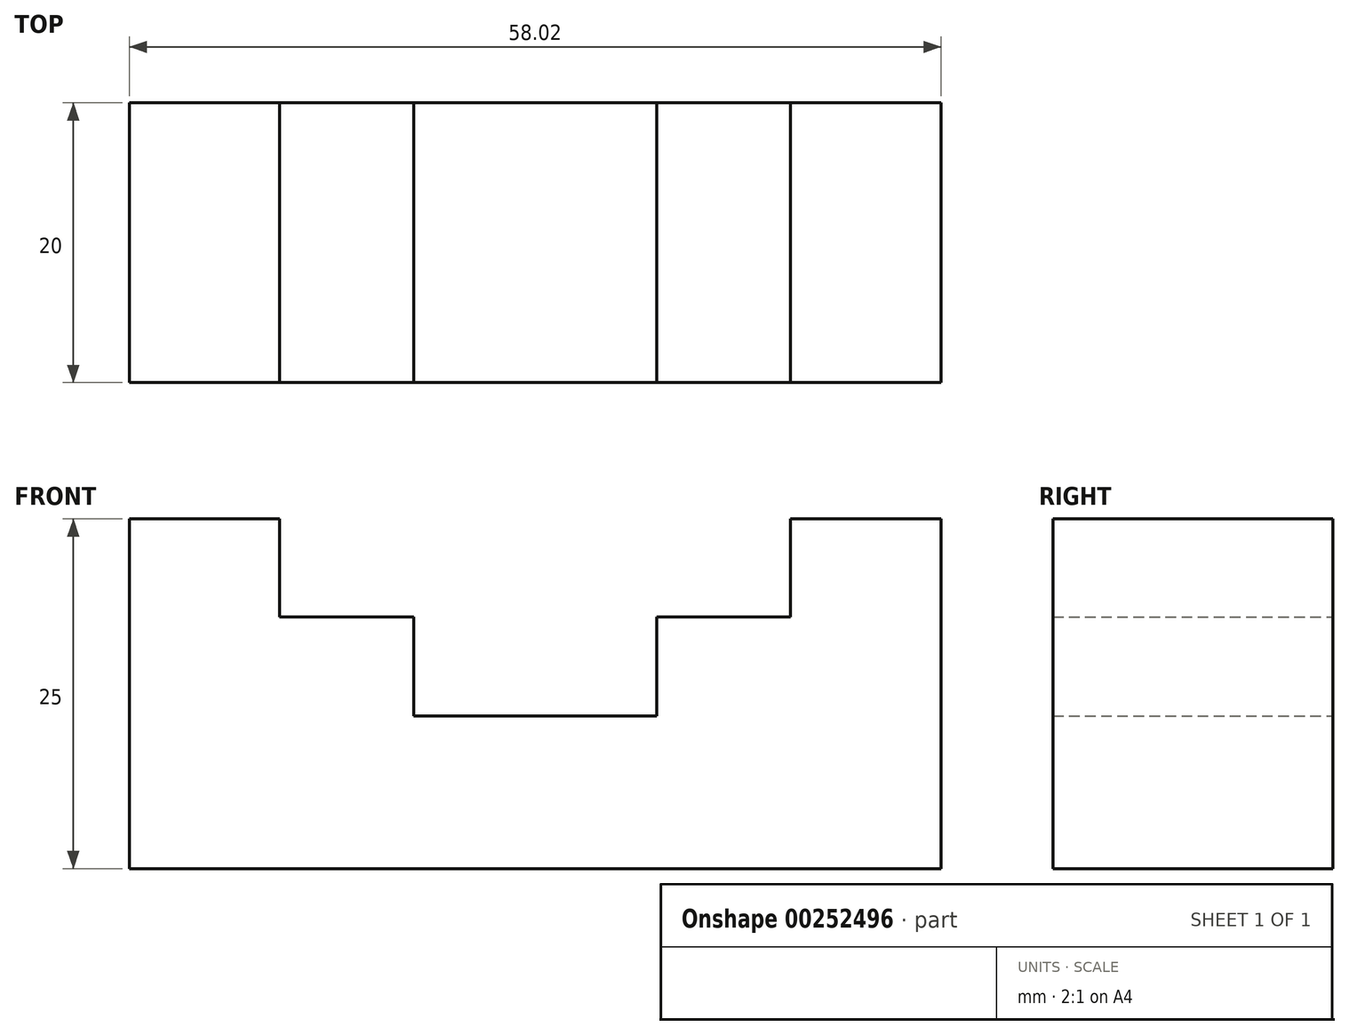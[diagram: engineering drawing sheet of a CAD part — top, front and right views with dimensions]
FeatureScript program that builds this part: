
annotation { "Feature Type Name" : "Feature", "Feature Type Description" : "" }
export const myFeature = defineFeature(function(context is Context, id is Id, definition is map)
    precondition{}
    {
        {
            var Q0;
            Q0=qCreatedBy(makeId("Front.planeOp"),FACE);
            var sketch = newSketch(context, id + "F0", { "sketchPlane" : qUnion([Q0])});
            skLineSegment(sketch, "E0.bottom", {"start": v(49.63, 71.5) * mm, "end": v(86.13, 71.5) * mm});
            skLineSegment(sketch, "E0.top", {"start": v(49.63, 64.5) * mm, "end": v(86.13, 64.5) * mm});
            skLineSegment(sketch, "E0.left", {"start": v(49.63, 71.5) * mm, "end": v(49.63, 64.5) * mm});
            skLineSegment(sketch, "E0.right", {"start": v(86.13, 71.5) * mm, "end": v(86.13, 64.5) * mm});
            skPoint(sketch, "E1", {"position": v(67.88, 64.5) * mm});
            skLineSegment(sketch, "E2.bottom", {"start": v(59.2, 64.5) * mm, "end": v(76.56, 64.5) * mm});
            skLineSegment(sketch, "E2.top", {"start": v(59.2, 57.4) * mm, "end": v(76.56, 57.4) * mm});
            skLineSegment(sketch, "E2.left", {"start": v(76.56, 57.4) * mm, "end": v(76.56, 64.5) * mm});
            skLineSegment(sketch, "E2.right", {"start": v(59.2, 57.4) * mm, "end": v(59.2, 64.5) * mm});
            skPoint(sketch, "E3", {"position": v(67.88, 57.4) * mm});
            skLineSegment(sketch, "E4.bottom", {"start": v(38.87, 71.5) * mm, "end": v(96.9, 71.5) * mm});
            skLineSegment(sketch, "E4.top", {"start": v(38.87, 46.5) * mm, "end": v(96.9, 46.5) * mm});
            skLineSegment(sketch, "E4.left", {"start": v(96.9, 71.5) * mm, "end": v(96.9, 46.5) * mm});
            skLineSegment(sketch, "E4.right", {"start": v(38.87, 71.5) * mm, "end": v(38.87, 46.5) * mm});
            skPoint(sketch, "E5", {"position": v(67.88, 71.5) * mm});
            skSolve(sketch);
        }
        {
            var Q0;
            {var subQ1=sQuery(id+"F0.wireOp",EDGE,"E0.left");Q0=makeQuery(id+"F0.imprint","IMPRINT",FACE,{"disambiguationData":[TD([[makeQuery(id+"F0.imprint","IMPRINT",EDGE,{"derivedFrom":subQ1}),-1.0]])]});}
            extrude(context, id + "F1", {"entities" : qUnion([Q0]), "depth" : 20 * mm});
        }
    });
